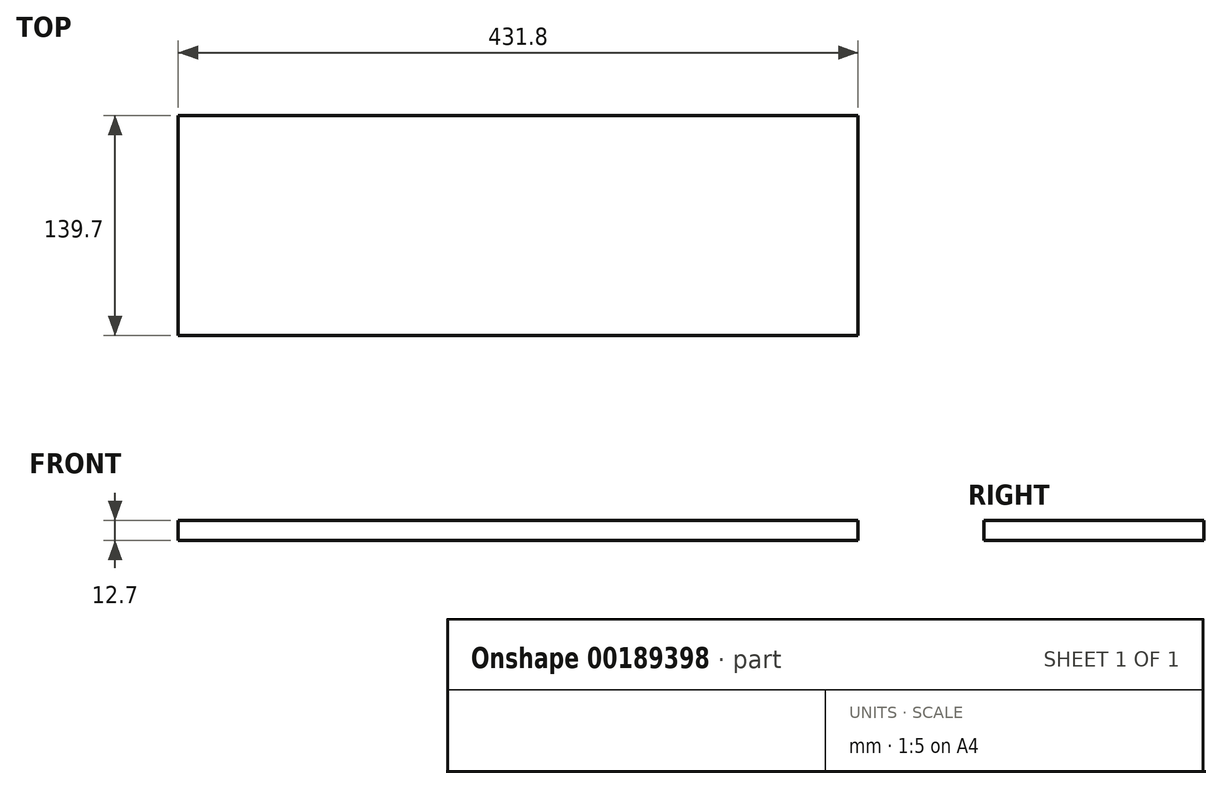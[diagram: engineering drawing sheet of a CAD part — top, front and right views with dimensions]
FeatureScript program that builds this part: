
annotation { "Feature Type Name" : "Feature", "Feature Type Description" : "" }
export const myFeature = defineFeature(function(context is Context, id is Id, definition is map)
    precondition{}
    {
        {
            var Q0;
            Q0=qCreatedBy(makeId("Right.planeOp"),FACE);
            var sketch = newSketch(context, id + "F0", { "sketchPlane" : qUnion([Q0])});
            skLineSegment(sketch, "E0.bottom", {"start": v(-69.85, 6.35) * mm, "end": v(69.85, 6.35) * mm});
            skLineSegment(sketch, "E0.top", {"start": v(-69.85, -6.35) * mm, "end": v(69.85, -6.35) * mm});
            skLineSegment(sketch, "E0.left", {"start": v(-69.85, 6.35) * mm, "end": v(-69.85, -6.35) * mm});
            skLineSegment(sketch, "E0.right", {"start": v(69.85, 6.35) * mm, "end": v(69.85, -6.35) * mm});
            skLineSegment(sketch, "E1", {"start": v(69.85, 6.35) * mm, "end": v(-69.85, -6.35) * mm, "construction": true});
            skSolve(sketch);
        }
        {
            var Q0;
            Q0 = qSketchRegion(id + "F0", true);
            extrude(context, id + "F1", {"entities" : qUnion([Q0]), "offsetDistance" : 25.4 * mm, "depth" : 228.6 * mm, "hasSecondDirection" : true, "secondDirectionOppositeDirection" : true, "secondDirectionDepth" : 203.2 * mm});
        }
    });
